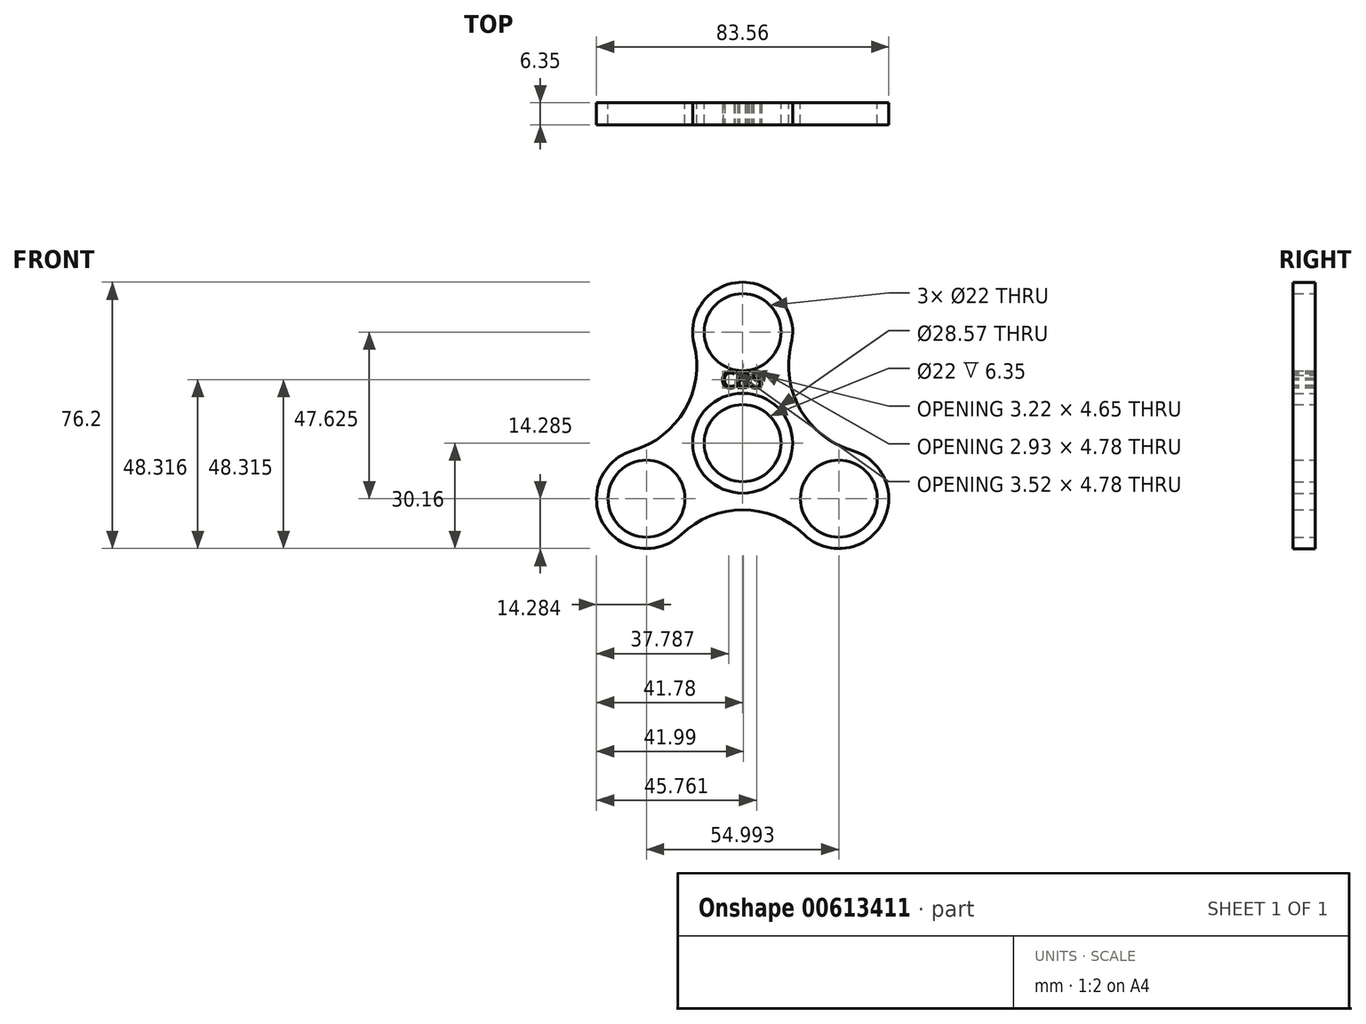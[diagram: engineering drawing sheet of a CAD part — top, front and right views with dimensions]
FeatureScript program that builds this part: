
annotation { "Feature Type Name" : "Feature", "Feature Type Description" : "" }
export const myFeature = defineFeature(function(context is Context, id is Id, definition is map)
    precondition{}
    {
        {
            var Q0;
            Q0=qCreatedBy(makeId("Front.planeOp"),FACE);
            var sketch = newSketch(context, id + "F0", { "sketchPlane" : qUnion([Q0])});
            skCircle(sketch, "E0", {"center": v(0, 0) * mm, "radius": 14.29 * mm});
            skCircle(sketch, "E1", {"center": v(0, 0) * mm, "radius": 11 * mm});
            skCircle(sketch, "E2", {"center": v(0, 31.75) * mm, "radius": 14.29 * mm});
            skCircle(sketch, "E3", {"center": v(0, 31.75) * mm, "radius": 11 * mm});
            skCircle(sketch, "E4.1.0", {"center": v(-27.5, -15.87) * mm, "radius": 14.29 * mm});
            skCircle(sketch, "E4.2.0", {"center": v(27.5, -15.88) * mm, "radius": 14.29 * mm});
            skCircle(sketch, "E5.1.0", {"center": v(-27.5, -15.87) * mm, "radius": 11 * mm});
            skCircle(sketch, "E5.2.0", {"center": v(27.5, -15.88) * mm, "radius": 11 * mm});
            skSolve(sketch);
        }
        {
            var Q0;
            Q0=qCreatedBy(makeId("Front.planeOp"),FACE);
            var sketch = newSketch(context, id + "F1", { "sketchPlane" : qUnion([Q0])});
            skArc(sketch, "E6", {"start": v(13.87, 28.33) * mm, "mid": v(16.54, 9.55) * mm, "end": v(31.47, -2.15) * mm});
            skArc(sketch, "E7", {"start": v(-31.47, -2.15) * mm, "mid": v(-16.54, 9.55) * mm, "end": v(-13.87, 28.33) * mm});
            skArc(sketch, "E8", {"start": v(17.6, -26.18) * mm, "mid": v(0, -19.1) * mm, "end": v(-17.6, -26.18) * mm});
            skCircle(sketch, "E9.0", {"center": v(0, 31.75) * mm, "radius": 14.29 * mm});
            skCircle(sketch, "E10.0", {"center": v(0, 31.75) * mm, "radius": 11 * mm});
            skCircle(sketch, "E11.0", {"center": v(0, 0) * mm, "radius": 14.29 * mm});
            skCircle(sketch, "E12.0", {"center": v(0, 0) * mm, "radius": 11 * mm});
            skCircle(sketch, "E13.0", {"center": v(27.5, -15.88) * mm, "radius": 14.29 * mm});
            skCircle(sketch, "E14.0", {"center": v(27.5, -15.88) * mm, "radius": 11 * mm});
            skCircle(sketch, "E15.0", {"center": v(-27.5, -15.87) * mm, "radius": 14.29 * mm});
            skCircle(sketch, "E16.0", {"center": v(-27.5, -15.87) * mm, "radius": 11 * mm});
            skSolve(sketch);
        }
        {
            var Q0;
            Q0 = qSketchRegion(id + "F1", true);
            var Q1;
            Q1=makeQuery(id+"F0.imprint","IMPRINT",FACE,{"disambiguationData":[TD([[makeQuery(id+"F0.imprint","IMPRINT",EDGE,{"derivedFrom":sQuery(id+"F0.wireOp",EDGE,"E0")}),1.0]])]});
            extrude(context, id + "F2", {"entities" : qUnion([Q0, Q1]), "depth" : 6.35 * mm, "offsetDistance" : 25.4 * mm});
        }
        {
            var Q0;
            Q0=makeQuery(id+"F2.opExtrude","CAP_FACE",FACE,{"disambiguationData":[OSD([sQuery(id+"F1.wireOp",EDGE,"E6"),sQuery(id+"F1.wireOp",EDGE,"E7"),sQuery(id+"F1.wireOp",EDGE,"E8"),sQuery(id+"F1.wireOp",EDGE,"E9.0"),sQuery(id+"F1.wireOp",EDGE,"E10.0"),sQuery(id+"F1.wireOp",EDGE,"E11.0"),sQuery(id+"F1.wireOp",EDGE,"E13.0"),sQuery(id+"F1.wireOp",EDGE,"E14.0"),sQuery(id+"F1.wireOp",EDGE,"E15.0"),sQuery(id+"F1.wireOp",EDGE,"E16.0")])],"isStart":false});
            var sketch = newSketch(context, id + "F3", { "sketchPlane" : qUnion([Q0])});
            skText(sketch, "E17", { "text": "CBS", "fontName": "OpenSans-Regular.ttf"});
            const initialGuessF3  = {"E17": [-0.00615, 0.01583, 1, 0, 0.00469]};
            skSetInitialGuess(sketch, initialGuessF3);
            skSolve(sketch);
        }
        {
            var Q0;
            Q0 = qSketchRegion(id + "F3", true);
            extrude(context, id + "F4", {"entities" : qUnion([Q0]), "operationType" : NewBodyOperationType.REMOVE, "oppositeDirection" : true, "depth" : 6.35 * mm, "offsetDistance" : 25.4 * mm});
        }
    });
